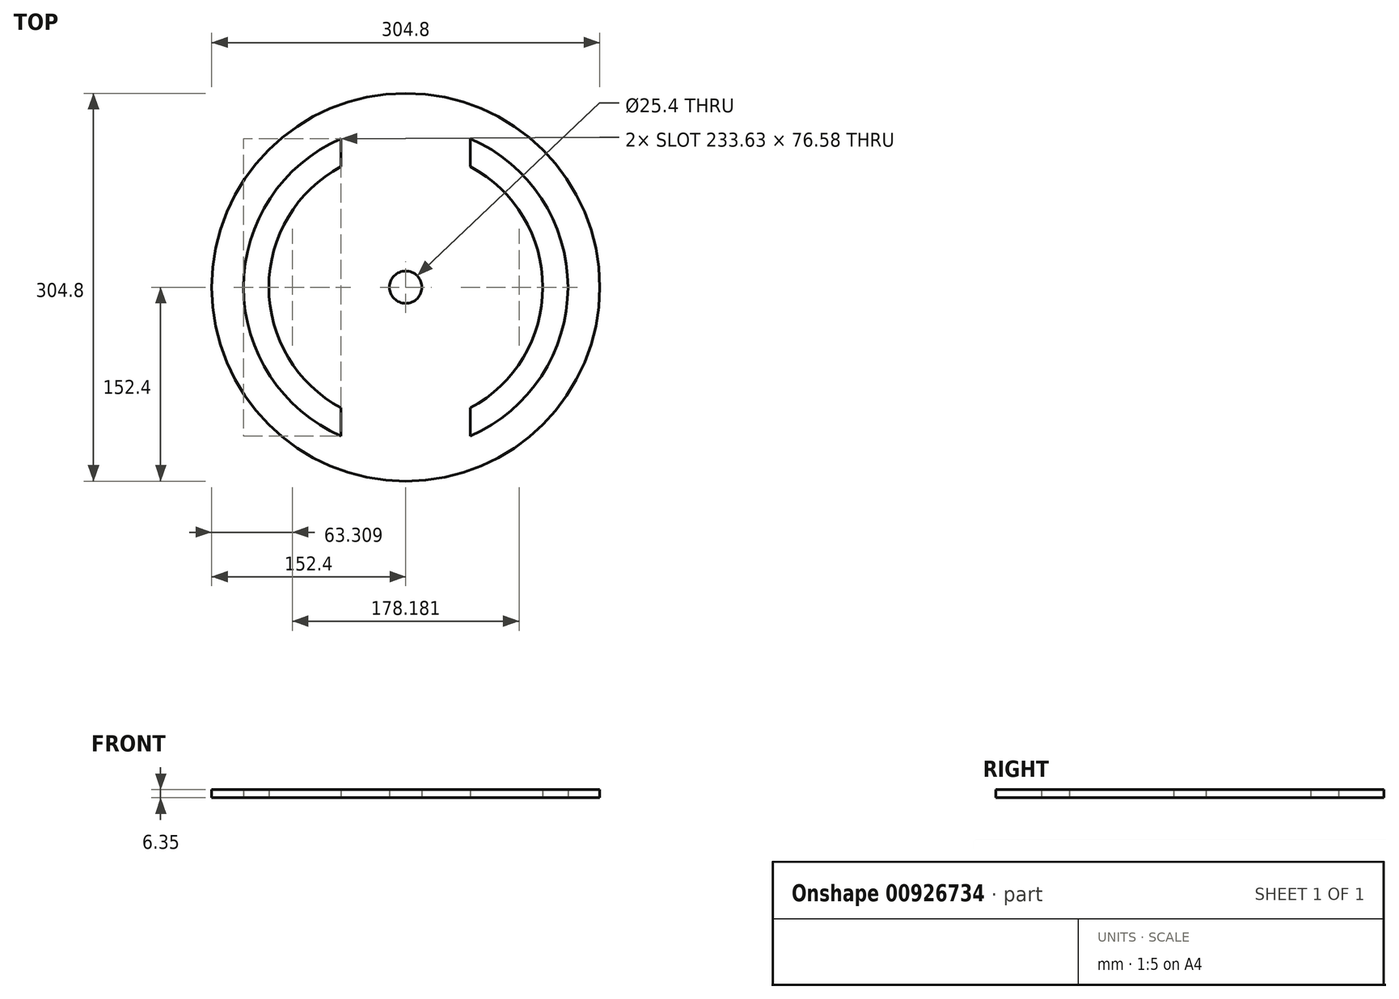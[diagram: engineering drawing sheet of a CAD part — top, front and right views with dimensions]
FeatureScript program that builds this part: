
annotation { "Feature Type Name" : "Feature", "Feature Type Description" : "" }
export const myFeature = defineFeature(function(context is Context, id is Id, definition is map)
    precondition{}
    {
        {
            var Q0;
            Q0=qCreatedBy(makeId("Top.planeOp"),FACE);
            var sketch = newSketch(context, id + "F0", { "sketchPlane" : qUnion([Q0])});
            skArc(sketch, "E0", {"start": v(-50.8, 116.81) * mm, "mid": v(-127.38, 0) * mm, "end": v(-50.8, -116.81) * mm});
            skCircle(sketch, "E1", {"center": v(0, 0) * mm, "radius": 152.4 * mm});
            skArc(sketch, "E2", {"start": v(-50.8, 94.82) * mm, "mid": v(-107.57, 0) * mm, "end": v(-50.8, -94.82) * mm});
            skLineSegment(sketch, "E3", {"start": v(-50.8, 116.81) * mm, "end": v(-50.8, 94.82) * mm});
            skLineSegment(sketch, "E4.trimOffspring", {"start": v(-50.8, -94.82) * mm, "end": v(-50.8, -116.81) * mm});
            skLineSegment(sketch, "E5.MirrorCS", {"start": v(50.8, 116.81) * mm, "end": v(50.8, 94.82) * mm});
            skArc(sketch, "E6.MirrorCS", {"start": v(50.8, 116.81) * mm, "mid": v(127.38, 0) * mm, "end": v(50.8, -116.81) * mm});
            skArc(sketch, "E7.MirrorCS", {"start": v(50.8, 94.82) * mm, "mid": v(107.57, 0) * mm, "end": v(50.8, -94.82) * mm});
            skLineSegment(sketch, "E8.MirrorCS", {"start": v(50.8, -94.82) * mm, "end": v(50.8, -116.81) * mm});
            skLineSegment(sketch, "E9", {"start": v(-152.4, 0) * mm, "end": v(152.4, 0) * mm, "construction": true});
            skCircle(sketch, "E10", {"center": v(0, 0) * mm, "radius": 12.7 * mm});
            skSolve(sketch);
        }
        {
            var Q0;
            Q0=qSketchRegion(id+"F0",true);
            extrude(context, id + "F1", {"entities" : qUnion([Q0]), "depth" : 6.35 * mm, "offsetDistance" : 25.4 * mm});
        }
    });
